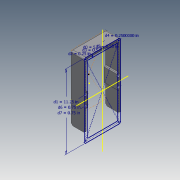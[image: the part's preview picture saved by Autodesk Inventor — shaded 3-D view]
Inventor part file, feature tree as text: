
AUTODESK INVENTOR PART (.ipt)
format: ipt  version: 2020.3 (Build 243373000, 373)  size: 219,136 bytes
history: native  units: in
note: dims shown in document units (in); Inventor stores cm internally (conversion verified against a paired STEP export)
features: sketch x6, extrude x4, fillet x2, hole x2, chamfer x2, projected_geometry x2
ambient origin geometry x8: Origin, YZ Plane, XZ Plane, XY Plane, X Axis, Y Axis, Z Axis, Center Point
bodies: Solid1 (feature_tree)
feature tree (18):
  sketch  "Sketch1"  dims[d0=5.5in d1=11.25in d2=0.25in]
  extrude  "Extrusion1"  Depth=0.25in
  fillet  "Fillet1"  Radius=0.25in
  hole  "Hole1"  [1 undecoded]
  extrude  "Extrusion2"  Depth=0.25in
  hole  "Hole2"  [1 undecoded]
  chamfer  "Chamfer1"  [1 undecoded]
  extrude  "Extrusion3"  TaperAngle=0.0deg  [1 undecoded]
  extrude  "Extrusion4"  Depth=0.3in
  fillet  "Fillet2"  Radius=0.3in
  chamfer  "Chamfer2"  Distance=0.3in
  sketch  "Sketch6"  dims[d11=0.21in d12=0.394in d13=0.4in d14=0.35in d15=0.5635in d16=0.559in d17=0.8108in d18=0.0in d19=0.0in d20=0.0in d21=0.3in d22=0.3in d23=0.3in d24=0.3in d25=0.126in d26=0.75in d27=0.15in d28=0.2in d29=0.5635in d30=0.75in d31=0.8108in d32=0.025in d33=0.125in d34=45.0deg d35=9.75in d36=0.0in d37=0.0in d38=0.2in d39=2.25in d40=1.15in d41=0.0in d42=0.125in d43=0.25in d44=0.125in d45=45.0deg]
  sketch  "Sketch2"  dims[d3=0.5in d4=0.25in]
  sketch  "Sketch3"  dims[d5=0.25in d6=0.75in]
  projected_geometry  "Projected Loop1"
  projected_geometry  "Projected Loop2"
  sketch  "Sketch4"  dims[d7=0.75in d8=1.95in d9=0.0in]
  sketch  "Sketch5"  dims[d10=0.25in]
note: 4 required parameter values undecoded (feature->parameter linkage not recoverable at this tier; creation-order binding heuristic only, values carry confidence <= 0.55)
